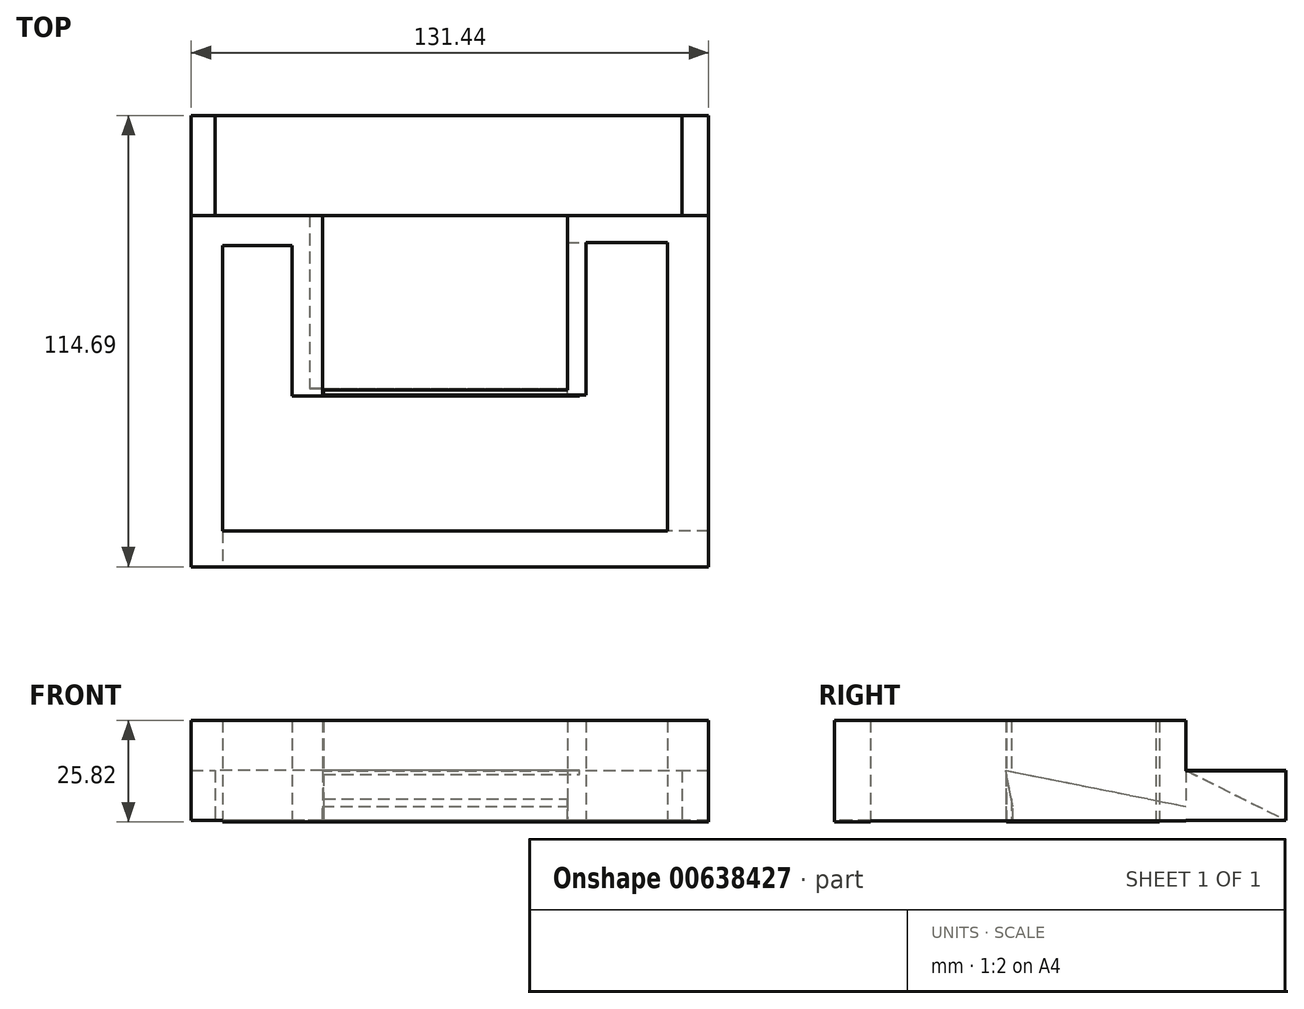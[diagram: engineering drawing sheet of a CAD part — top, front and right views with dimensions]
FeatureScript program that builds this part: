
annotation { "Feature Type Name" : "Feature", "Feature Type Description" : "" }
export const myFeature = defineFeature(function(context is Context, id is Id, definition is map)
    precondition{}
    {
        {
            var Q0;
            Q0=qCreatedBy(makeId("Top.planeOp"),FACE);
            var sketch = newSketch(context, id + "F0", { "sketchPlane" : qUnion([Q0])});
            skLineSegment(sketch, "E0.bottom", {"start": v(-65.72, 44.37) * mm, "end": v(-57.81, 44.37) * mm});
            skLineSegment(sketch, "E0.top", {"start": v(-65.72, -44.9) * mm, "end": v(-57.81, -44.9) * mm});
            skLineSegment(sketch, "E0.left", {"start": v(-65.72, 44.37) * mm, "end": v(-65.72, -44.9) * mm});
            skLineSegment(sketch, "E0.right", {"start": v(-57.81, 44.37) * mm, "end": v(-57.81, -44.9) * mm});
            skSolve(sketch);
        }
        {
            var Q0;
            Q0 = qSketchRegion(id + "F0", true);
            extrude(context, id + "F1", {"entities" : qUnion([Q0]), "depth" : 25.4 * mm, "offsetDistance" : 25.4 * mm});
        }
        {
            var Q0;
            Q0=makeQuery(id+"F1.opExtrude","SWEPT_FACE",FACE,{"disambiguationData":[OSD([sQuery(id+"F0.wireOp",EDGE,"E0.right")])]});
            var sketch = newSketch(context, id + "F2", { "sketchPlane" : qUnion([Q0])});
            skLineSegment(sketch, "E1.bottom", {"start": v(-44.9, 25.4) * mm, "end": v(-35.84, 25.4) * mm});
            skLineSegment(sketch, "E1.top", {"start": v(-44.9, -0.42) * mm, "end": v(-35.84, -0.42) * mm});
            skLineSegment(sketch, "E1.left", {"start": v(-44.9, 25.4) * mm, "end": v(-44.9, -0.42) * mm});
            skLineSegment(sketch, "E1.right", {"start": v(-35.84, 25.4) * mm, "end": v(-35.84, -0.42) * mm});
            skSolve(sketch);
        }
        {
            var Q0;
            Q0 = qSketchRegion(id + "F2", true);
            extrude(context, id + "F3", {"entities" : qUnion([Q0]), "operationType" : NewBodyOperationType.ADD, "depth" : 123.53 * mm, "offsetDistance" : 25.4 * mm});
        }
        {
            var Q0;
            Q0=makeQuery(id+"F3.opExtrude","SWEPT_FACE",FACE,{"disambiguationData":[OSD([sQuery(id+"F2.wireOp",EDGE,"E1.right")])]});
            var sketch = newSketch(context, id + "F4", { "sketchPlane" : qUnion([Q0])});
            skLineSegment(sketch, "E2.bottom", {"start": v(-65.72, 25.4) * mm, "end": v(-55.2, 25.4) * mm});
            skLineSegment(sketch, "E2.top", {"start": v(-65.72, -0.2) * mm, "end": v(-55.2, -0.2) * mm});
            skLineSegment(sketch, "E2.left", {"start": v(-65.72, 25.4) * mm, "end": v(-65.72, -0.2) * mm});
            skLineSegment(sketch, "E2.right", {"start": v(-55.2, 25.4) * mm, "end": v(-55.2, -0.2) * mm});
            skSolve(sketch);
        }
        {
            var Q0;
            Q0 = qSketchRegion(id + "F4", true);
            extrude(context, id + "F5", {"entities" : qUnion([Q0]), "operationType" : NewBodyOperationType.ADD, "depth" : 80.23 * mm, "offsetDistance" : 25.4 * mm});
        }
        {
            var Q0;
            Q0=makeQuery(id+"F5.opExtrude","SWEPT_FACE",FACE,{"disambiguationData":[OSD([sQuery(id+"F4.wireOp",EDGE,"E2.right")])]});
            var sketch = newSketch(context, id + "F6", { "sketchPlane" : qUnion([Q0])});
            skLineSegment(sketch, "E3.bottom", {"start": v(-37.55, 25.4) * mm, "end": v(-44.4, 25.4) * mm});
            skLineSegment(sketch, "E3.top", {"start": v(-37.55, -0.2) * mm, "end": v(-44.4, -0.2) * mm});
            skLineSegment(sketch, "E3.left", {"start": v(-37.55, 25.4) * mm, "end": v(-37.55, -0.2) * mm});
            skLineSegment(sketch, "E3.right", {"start": v(-44.4, 25.4) * mm, "end": v(-44.4, -0.2) * mm});
            skSolve(sketch);
        }
        {
            var Q0;
            Q0 = qSketchRegion(id + "F6", true);
            extrude(context, id + "F7", {"entities" : qUnion([Q0]), "operationType" : NewBodyOperationType.ADD, "depth" : 25.4 * mm, "offsetDistance" : 25.4 * mm});
        }
        {
            var Q0;
            Q0=makeQuery(id+"F1.opExtrude","SWEPT_FACE",FACE,{"disambiguationData":[OSD([sQuery(id+"F0.wireOp",EDGE,"E0.right")])]});
            var sketch = newSketch(context, id + "F8", { "sketchPlane" : qUnion([Q0])});
            skLineSegment(sketch, "E4.bottom", {"start": v(44.37, 25.4) * mm, "end": v(36.69, 25.4) * mm});
            skLineSegment(sketch, "E4.top", {"start": v(44.37, 0) * mm, "end": v(36.69, 0) * mm});
            skLineSegment(sketch, "E4.left", {"start": v(44.37, 25.4) * mm, "end": v(44.37, 0) * mm});
            skLineSegment(sketch, "E4.right", {"start": v(36.69, 25.4) * mm, "end": v(36.69, 0) * mm});
            skSolve(sketch);
        }
        {
            var Q0;
            Q0 = qSketchRegion(id + "F8", true);
            extrude(context, id + "F9", {"entities" : qUnion([Q0]), "operationType" : NewBodyOperationType.ADD, "depth" : 25.4 * mm, "offsetDistance" : 25.4 * mm});
        }
        {
            var Q0;
            Q0=makeQuery(id+"F7.opExtrude","SWEPT_FACE",FACE,{"disambiguationData":[OSD([sQuery(id+"F6.wireOp",EDGE,"E3.left")])]});
            var sketch = newSketch(context, id + "F10", { "sketchPlane" : qUnion([Q0])});
            skLineSegment(sketch, "E5.bottom", {"start": v(29.8, 25.4) * mm, "end": v(34.51, 25.4) * mm});
            skLineSegment(sketch, "E5.top", {"start": v(29.8, -0.34) * mm, "end": v(34.51, -0.34) * mm});
            skLineSegment(sketch, "E5.left", {"start": v(29.8, 25.4) * mm, "end": v(29.8, -0.34) * mm});
            skLineSegment(sketch, "E5.right", {"start": v(34.51, 25.4) * mm, "end": v(34.51, -0.34) * mm});
            skSolve(sketch);
        }
        {
            var Q0;
            Q0 = qSketchRegion(id + "F10", true);
            extrude(context, id + "F11", {"entities" : qUnion([Q0]), "operationType" : NewBodyOperationType.ADD, "depth" : 38.8 * mm, "offsetDistance" : 25.4 * mm});
        }
        {
            var Q0;
            Q0=makeQuery(id+"F11.boolean.opBoolean","MERGE",FACE,{"derivedFrom":[makeQuery(id+"F7.opExtrude","CAP_FACE",FACE,{"disambiguationData":[OSD([sQuery(id+"F6.wireOp",EDGE,"E3.bottom"),sQuery(id+"F6.wireOp",EDGE,"E3.top"),sQuery(id+"F6.wireOp",EDGE,"E3.left"),sQuery(id+"F6.wireOp",EDGE,"E3.right")])],"isStart":false}),makeQuery(id+"F11.opExtrude","SWEPT_FACE",FACE,{"disambiguationData":[OSD([sQuery(id+"F10.wireOp",EDGE,"E5.left")])]})]});
            var sketch = newSketch(context, id + "F12", { "sketchPlane" : qUnion([Q0])});
            skLineSegment(sketch, "E6.bottom", {"start": v(1.25, 25.4) * mm, "end": v(0, 25.4) * mm});
            skLineSegment(sketch, "E6.top", {"start": v(1.25, 0) * mm, "end": v(0, 0) * mm});
            skLineSegment(sketch, "E6.left", {"start": v(1.25, 25.4) * mm, "end": v(1.25, 0) * mm});
            skLineSegment(sketch, "E6.right", {"start": v(0, 25.4) * mm, "end": v(0, 0) * mm});
            skSolve(sketch);
        }
        {
            var Q0;
            Q0 = qSketchRegion(id + "F12", true);
            extrude(context, id + "F13", {"entities" : qUnion([Q0]), "operationType" : NewBodyOperationType.ADD, "depth" : 61.9 * mm, "offsetDistance" : 25.4 * mm});
        }
        {
            var Q0;
            Q0=makeQuery(id+"F9.opExtrude","SWEPT_FACE",FACE,{"disambiguationData":[OSD([sQuery(id+"F8.wireOp",EDGE,"E4.right")])]});
            var sketch = newSketch(context, id + "F14", { "sketchPlane" : qUnion([Q0])});
            skLineSegment(sketch, "E7.bottom", {"start": v(-32.41, 25.4) * mm, "end": v(-40.16, 25.4) * mm});
            skLineSegment(sketch, "E7.top", {"start": v(-32.41, 0) * mm, "end": v(-40.16, 0) * mm});
            skLineSegment(sketch, "E7.left", {"start": v(-32.41, 25.4) * mm, "end": v(-32.41, 0) * mm});
            skLineSegment(sketch, "E7.right", {"start": v(-40.16, 25.4) * mm, "end": v(-40.16, 0) * mm});
            skSolve(sketch);
        }
        {
            var Q0;
            Q0 = qSketchRegion(id + "F14", true);
            extrude(context, id + "F15", {"entities" : qUnion([Q0]), "operationType" : NewBodyOperationType.ADD, "depth" : 38.13 * mm, "offsetDistance" : 25.4 * mm});
        }
        {
            var Q0;
            Q0=makeQuery(id+"F11.boolean.opBoolean","MERGE",FACE,{"derivedFrom":[makeQuery(id+"F7.opExtrude","CAP_FACE",FACE,{"disambiguationData":[OSD([sQuery(id+"F6.wireOp",EDGE,"E3.bottom"),sQuery(id+"F6.wireOp",EDGE,"E3.top"),sQuery(id+"F6.wireOp",EDGE,"E3.left"),sQuery(id+"F6.wireOp",EDGE,"E3.right")])],"isStart":false}),makeQuery(id+"F11.opExtrude","SWEPT_FACE",FACE,{"disambiguationData":[OSD([sQuery(id+"F10.wireOp",EDGE,"E5.left")])]})]});
            var sketch = newSketch(context, id + "F16", { "sketchPlane" : qUnion([Q0])});
            skLineSegment(sketch, "E8.bottom", {"start": v(-44.4, -0.2) * mm, "end": v(-0.37, -0.2) * mm});
            skLineSegment(sketch, "E8.top", {"start": v(-44.4, 3.56) * mm, "end": v(-0.37, 3.56) * mm});
            skLineSegment(sketch, "E8.left", {"start": v(-44.4, -0.2) * mm, "end": v(-44.4, 3.56) * mm});
            skLineSegment(sketch, "E8.right", {"start": v(-0.37, -0.2) * mm, "end": v(-0.37, 3.56) * mm});
            skSolve(sketch);
        }
        {
            var Q0;
            Q0 = qSketchRegion(id + "F16", true);
            extrude(context, id + "F17", {"entities" : qUnion([Q0]), "operationType" : NewBodyOperationType.ADD, "depth" : 65.47 * mm, "offsetDistance" : 25.4 * mm});
        }
        {
            var Q0;
            Q0=makeQuery(id+"F15.boolean.opBoolean","MERGE",FACE,{"derivedFrom":[makeQuery(id+"F9.opExtrude","CAP_FACE",FACE,{"disambiguationData":[OSD([sQuery(id+"F8.wireOp",EDGE,"E4.bottom"),sQuery(id+"F8.wireOp",EDGE,"E4.top"),sQuery(id+"F8.wireOp",EDGE,"E4.left"),sQuery(id+"F8.wireOp",EDGE,"E4.right")])],"isStart":false}),makeQuery(id+"F15.opExtrude","SWEPT_FACE",FACE,{"disambiguationData":[OSD([sQuery(id+"F14.wireOp",EDGE,"E7.left")])]})]});
            var sketch = newSketch(context, id + "F18", { "sketchPlane" : qUnion([Q0])});
            skLineSegment(sketch, "E9", {"start": v(-1.45, 12.7) * mm, "end": v(44.37, 3.56) * mm});
            skLineSegment(sketch, "E10", {"start": v(44.37, 3.56) * mm, "end": v(-1.45, 12.7) * mm});
            skLineSegment(sketch, "E11", {"start": v(0.37, 3.56) * mm, "end": v(-1.45, 12.7) * mm});
            skLineSegment(sketch, "E12", {"start": v(0.37, 3.56) * mm, "end": v(44.37, 3.56) * mm});
            skSolve(sketch);
        }
        {
            var Q0;
            Q0 = qSketchRegion(id + "F18", true);
            extrude(context, id + "F19", {"entities" : qUnion([Q0]), "operationType" : NewBodyOperationType.ADD, "depth" : 65.3 * mm, "offsetDistance" : 25.4 * mm});
        }
        {
            var Q0;
            Q0=makeQuery(id+"F9.boolean.opBoolean","MERGE",FACE,{"derivedFrom":[makeQuery(id+"F1.opExtrude","SWEPT_FACE",FACE,{"disambiguationData":[OSD([sQuery(id+"F0.wireOp",EDGE,"E0.bottom")])]}),makeQuery(id+"F9.opExtrude","SWEPT_FACE",FACE,{"disambiguationData":[OSD([sQuery(id+"F8.wireOp",EDGE,"E4.left")])]})]});
            var sketch = newSketch(context, id + "F20", { "sketchPlane" : qUnion([Q0])});
            skLineSegment(sketch, "E13.bottom", {"start": v(65.72, 12.7) * mm, "end": v(59.73, 12.7) * mm});
            skLineSegment(sketch, "E13.top", {"start": v(65.72, 0) * mm, "end": v(59.73, 0) * mm});
            skLineSegment(sketch, "E13.left", {"start": v(65.72, 12.7) * mm, "end": v(65.72, 0) * mm});
            skLineSegment(sketch, "E13.right", {"start": v(59.73, 12.7) * mm, "end": v(59.73, 0) * mm});
            skSolve(sketch);
        }
        {
            var Q0;
            Q0 = qSketchRegion(id + "F20", true);
            extrude(context, id + "F21", {"entities" : qUnion([Q0]), "operationType" : NewBodyOperationType.ADD, "depth" : 25.4 * mm, "offsetDistance" : 25.4 * mm});
        }
        {
            var Q0;
            Q0=makeQuery(id+"F21.opExtrude","SWEPT_FACE",FACE,{"disambiguationData":[OSD([sQuery(id+"F20.wireOp",EDGE,"E13.right")])]});
            var sketch = newSketch(context, id + "F22", { "sketchPlane" : qUnion([Q0])});
            skLineSegment(sketch, "E14", {"start": v(44.37, 12.7) * mm, "end": v(69.77, 0) * mm});
            skLineSegment(sketch, "E15", {"start": v(69.77, 0) * mm, "end": v(69.77, 0) * mm});
            skLineSegment(sketch, "E16", {"start": v(44.37, 0) * mm, "end": v(69.77, 0) * mm});
            skLineSegment(sketch, "E17", {"start": v(44.37, 0) * mm, "end": v(44.37, 12.7) * mm});
            skSolve(sketch);
        }
        {
            var Q0;
            Q0 = qSketchRegion(id + "F22", true);
            extrude(context, id + "F23", {"entities" : qUnion([Q0]), "operationType" : NewBodyOperationType.ADD, "depth" : 118.61 * mm, "offsetDistance" : 25.4 * mm});
        }
        {
            var Q0;
            Q0=makeQuery(id+"F17.boolean.opBoolean","MERGE",FACE,{"derivedFrom":[makeQuery(id+"F7.boolean.opBoolean","MERGE",FACE,{"derivedFrom":[makeQuery(id+"F5.opExtrude","CAP_FACE",FACE,{"disambiguationData":[OSD([sQuery(id+"F4.wireOp",EDGE,"E2.bottom"),sQuery(id+"F4.wireOp",EDGE,"E2.top"),sQuery(id+"F4.wireOp",EDGE,"E2.left"),sQuery(id+"F4.wireOp",EDGE,"E2.right")])],"isStart":false}),makeQuery(id+"F7.opExtrude","SWEPT_FACE",FACE,{"disambiguationData":[OSD([sQuery(id+"F6.wireOp",EDGE,"E3.right")])]})]}),makeQuery(id+"F17.opExtrude","SWEPT_FACE",FACE,{"disambiguationData":[OSD([sQuery(id+"F16.wireOp",EDGE,"E8.left")])]})]});
            var sketch = newSketch(context, id + "F24", { "sketchPlane" : qUnion([Q0])});
            skLineSegment(sketch, "E18.bottom", {"start": v(-65.72, 12.6) * mm, "end": v(-58.88, 12.6) * mm});
            skLineSegment(sketch, "E18.top", {"start": v(-65.72, 0) * mm, "end": v(-58.88, 0) * mm});
            skLineSegment(sketch, "E18.left", {"start": v(-65.72, 12.6) * mm, "end": v(-65.72, 0) * mm});
            skLineSegment(sketch, "E18.right", {"start": v(-58.88, 12.6) * mm, "end": v(-58.88, 0) * mm});
            skSolve(sketch);
        }
        {
            var Q0;
            Q0 = qSketchRegion(id + "F24", true);
            extrude(context, id + "F25", {"entities" : qUnion([Q0]), "operationType" : NewBodyOperationType.ADD, "depth" : 25.4 * mm, "offsetDistance" : 25.4 * mm});
        }
    });
